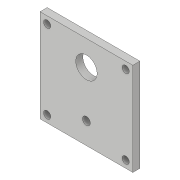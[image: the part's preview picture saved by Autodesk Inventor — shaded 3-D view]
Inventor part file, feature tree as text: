
AUTODESK INVENTOR PART (.ipt)
format: ipt  version: 2019 (Build 230136000, 136)  size: 115,712 bytes
history: native  units: in
note: dims shown in document units (in); Inventor stores cm internally (conversion verified against a paired STEP export)
features: extrude x3, sketch x3
ambient origin geometry x8: Origin, YZ Plane, XZ Plane, XY Plane, X Axis, Y Axis, Z Axis, Center Point
bodies: Solid1 (feature_tree)
feature tree (6):
  extrude  "Extrusion1"  Depth=5.1181in
  extrude  "Extrusion2"  Depth=0.3937in
  extrude  "Extrusion3"  Depth=0.3937in
  sketch  "Sketch1"  dims[d0=5.1181in d1=5.1181in]
  sketch  "Sketch2"  dims[d2=0.3937in d3=0.0in d4=0.3937in]
  sketch  "Sketch3"  dims[d5=4.7244in d6=4.3307in d7=4.3307in d8=4.3307in d9=0.3937in d10=0.3937in d11=0.3937in d12=0.3937in d13=0.3937in d14=0.0in d15=2.5591in d16=1.1811in d17=0.4331in d18=2.5591in d19=1.378in d20=1.1811in d21=0.3937in d22=0.0in]
